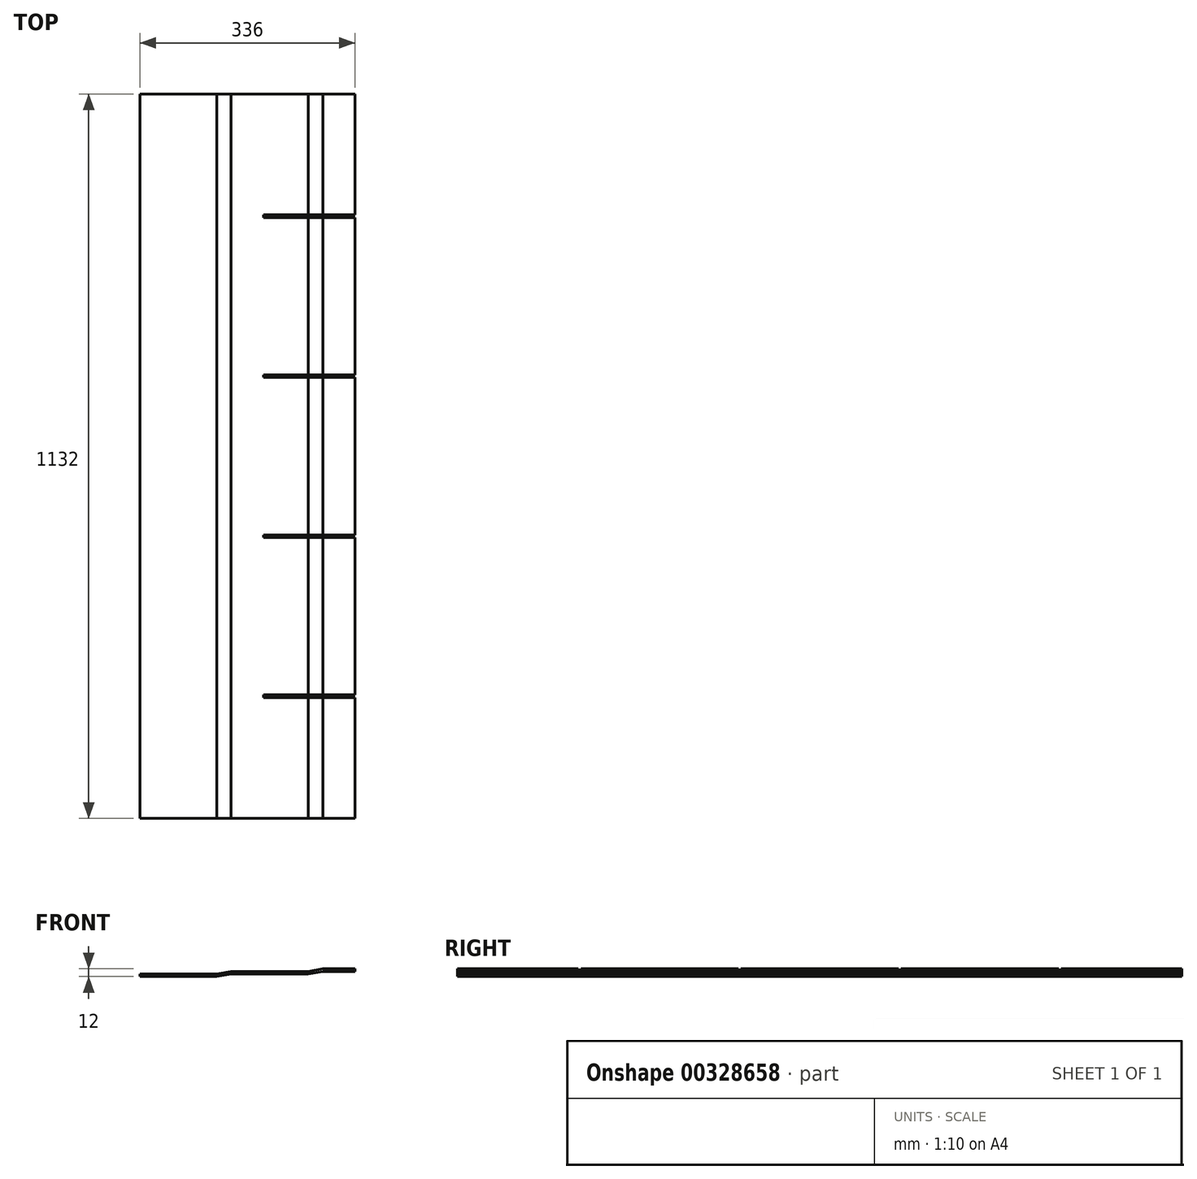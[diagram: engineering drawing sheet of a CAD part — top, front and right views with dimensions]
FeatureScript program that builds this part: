
annotation { "Feature Type Name" : "Feature", "Feature Type Description" : "" }
export const myFeature = defineFeature(function(context is Context, id is Id, definition is map)
    precondition{}
    {
        {
            var Q0;
            Q0=qCreatedBy(makeId("Front.planeOp"),FACE);
            var sketch = newSketch(context, id + "F0", { "sketchPlane" : qUnion([Q0])});
            skLineSegment(sketch, "E0.bottom", {"start": v(0, 0) * mm, "end": v(119.96, 0) * mm});
            skLineSegment(sketch, "E0.top", {"start": v(0, -4) * mm, "end": v(120.31, -4) * mm});
            skLineSegment(sketch, "E0.left", {"start": v(0, 0) * mm, "end": v(0, -4) * mm});
            skLineSegment(sketch, "E1", {"start": v(336, 4) * mm, "end": v(286, 4) * mm});
            skLineSegment(sketch, "E2", {"start": v(142.65, 4) * mm, "end": v(119.96, 0) * mm});
            skLineSegment(sketch, "E3", {"start": v(143, 0) * mm, "end": v(120.31, -4) * mm});
            skLineSegment(sketch, "E4.trimOffspring", {"start": v(143, 0) * mm, "end": v(263.31, 0) * mm});
            skLineSegment(sketch, "E5", {"start": v(336, 4) * mm, "end": v(336, 8) * mm});
            skLineSegment(sketch, "E6", {"start": v(336, 8) * mm, "end": v(285.65, 8) * mm});
            skLineSegment(sketch, "E7", {"start": v(285.65, 8) * mm, "end": v(262.96, 4) * mm});
            skLineSegment(sketch, "E8", {"start": v(263.31, 0) * mm, "end": v(286, 4) * mm});
            skLineSegment(sketch, "E9.trimOffspring", {"start": v(262.96, 4) * mm, "end": v(142.65, 4) * mm});
            skSolve(sketch);
        }
        {
            var Q0;
            Q0=qSketchRegion(id+"F0",true);
            extrude(context, id + "F1", {"entities" : qUnion([Q0]), "oppositeDirection" : true, "depth" : 1132 * mm});
        }
        {
            var Q0;
            Q0=makeQuery(id+"F1.opExtrude","SWEPT_FACE",FACE,{"disambiguationData":[OSD([sQuery(id+"F0.wireOp",EDGE,"E9.trimOffspring")])]});
            var sketch = newSketch(context, id + "F2", { "sketchPlane" : qUnion([Q0])});
            skLineSegment(sketch, "E10", {"start": v(193, 189) * mm, "end": v(193, 193) * mm});
            skLineSegment(sketch, "E11", {"start": v(193, 193) * mm, "end": v(336, 193) * mm});
            skLineSegment(sketch, "E12", {"start": v(336, 193) * mm, "end": v(336, 189) * mm});
            skLineSegment(sketch, "E13", {"start": v(336, 189) * mm, "end": v(193, 189) * mm});
            skLineSegment(sketch, "E14.0.1.0", {"start": v(336, 443) * mm, "end": v(336, 439) * mm});
            skLineSegment(sketch, "E14.0.1.1", {"start": v(193, 439) * mm, "end": v(193, 443) * mm});
            skLineSegment(sketch, "E14.0.1.2", {"start": v(193, 443) * mm, "end": v(336, 443) * mm});
            skLineSegment(sketch, "E14.0.1.3", {"start": v(336, 439) * mm, "end": v(193, 439) * mm});
            skLineSegment(sketch, "E14.0.2.0", {"start": v(336, 693) * mm, "end": v(336, 689) * mm});
            skLineSegment(sketch, "E14.0.2.1", {"start": v(193, 689) * mm, "end": v(193, 693) * mm});
            skLineSegment(sketch, "E14.0.2.2", {"start": v(193, 693) * mm, "end": v(336, 693) * mm});
            skLineSegment(sketch, "E14.0.2.3", {"start": v(336, 689) * mm, "end": v(193, 689) * mm});
            skLineSegment(sketch, "E14.direction1", {"start": v(193, 189) * mm, "end": v(193, 189) * mm});
            skLineSegment(sketch, "E14.direction2", {"start": v(193, 189) * mm, "end": v(193, 439) * mm, "construction": true});
            skLineSegment(sketch, "E15.0.0.3", {"start": v(336, 943) * mm, "end": v(336, 939) * mm});
            skLineSegment(sketch, "E15.3.0.3", {"start": v(193, 939) * mm, "end": v(193, 943) * mm});
            skLineSegment(sketch, "E15.6.0.3", {"start": v(193, 943) * mm, "end": v(336, 943) * mm});
            skLineSegment(sketch, "E15.9.0.3", {"start": v(336, 939) * mm, "end": v(193, 939) * mm});
            skSolve(sketch);
        }
        {
            var Q0;
            Q0=qSketchRegion(id+"F2",true);
            extrude(context, id + "F3", {"entities" : qUnion([Q0]), "operationType" : NewBodyOperationType.REMOVE, "endBound" : BoundingType.THROUGH_ALL, "oppositeDirection" : true, "depth" : 25 * mm, "hasSecondDirection" : true, "secondDirectionBound" : SecondDirectionBoundingType.THROUGH_ALL, "secondDirectionOppositeDirection" : false, "secondDirectionDepth" : 25 * mm});
        }
    });
